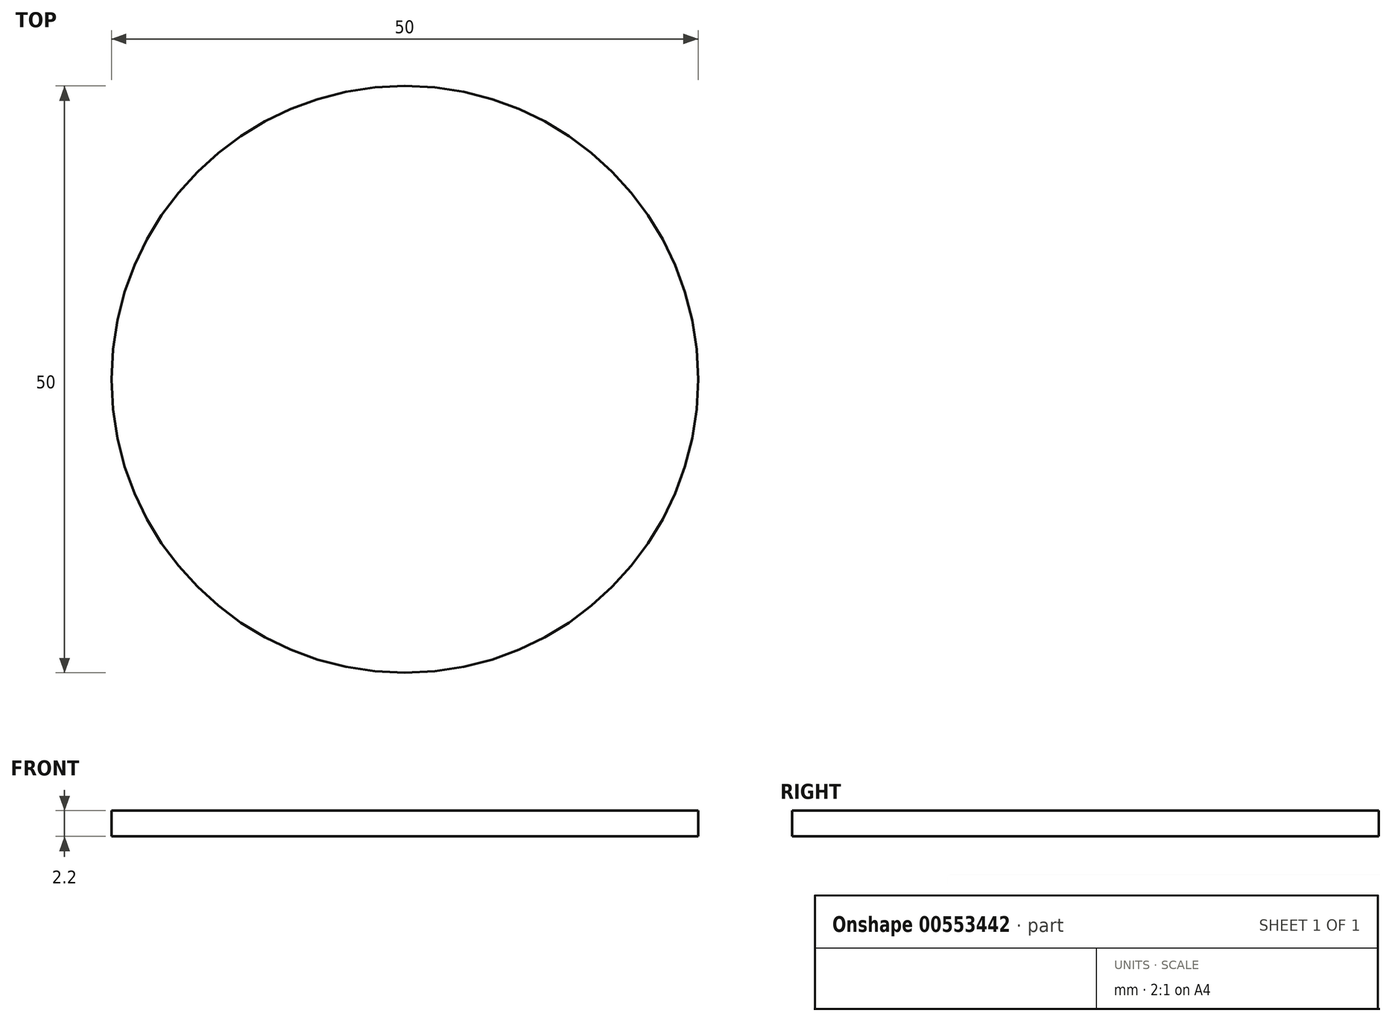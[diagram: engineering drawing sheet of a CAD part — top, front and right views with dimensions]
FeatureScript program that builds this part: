
annotation { "Feature Type Name" : "Feature", "Feature Type Description" : "" }
export const myFeature = defineFeature(function(context is Context, id is Id, definition is map)
    precondition{}
    {
        {
            var Q0;
            Q0=qCreatedBy(makeId("Top.planeOp"),FACE);
            var sketch = newSketch(context, id + "F0", { "sketchPlane" : qUnion([Q0])});
            skCircle(sketch, "E0", {"center": v(0, 0) * mm, "radius": 25 * mm});
            skSolve(sketch);
        }
        {
            var Q0;
            Q0 = qSketchRegion(id + "F0", true);
            extrude(context, id + "F1", {"entities" : qUnion([Q0]), "depth" : 2.2 * mm, "offsetDistance" : 25 * mm});
        }
    });
